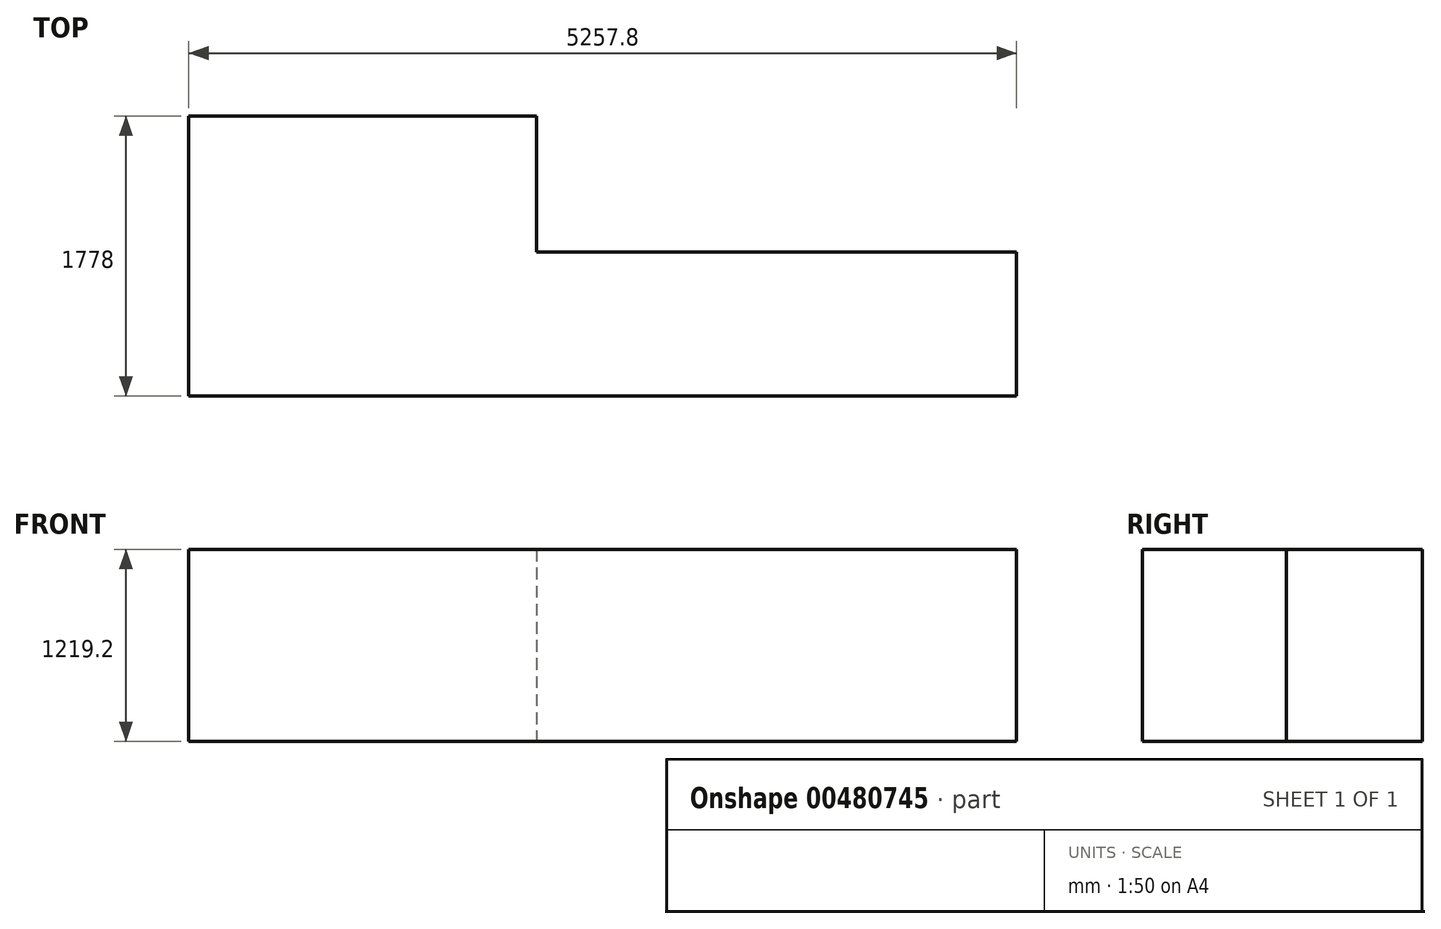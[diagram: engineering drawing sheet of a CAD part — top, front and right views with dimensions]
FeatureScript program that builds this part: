
annotation { "Feature Type Name" : "Feature", "Feature Type Description" : "" }
export const myFeature = defineFeature(function(context is Context, id is Id, definition is map)
    precondition{}
    {
        {
            var Q0;
            Q0=qCreatedBy(makeId("Top.planeOp"),FACE);
            var sketch = newSketch(context, id + "F0", { "sketchPlane" : qUnion([Q0])});
            skLineSegment(sketch, "E0.bottom", {"start": v(1104.9, 889) * mm, "end": v(-1104.9, 889) * mm});
            skLineSegment(sketch, "E0.top", {"start": v(1104.9, -889) * mm, "end": v(-1104.9, -889) * mm});
            skLineSegment(sketch, "E0.left", {"start": v(1104.9, 889) * mm, "end": v(1104.9, 25.4) * mm});
            skLineSegment(sketch, "E0.right", {"start": v(-1104.9, 889) * mm, "end": v(-1104.9, -889) * mm});
            skPoint(sketch, "E0.middle", {"position": v(0, 0) * mm});
            skLineSegment(sketch, "E1", {"start": v(1104.9, -889) * mm, "end": v(4152.9, -889) * mm});
            skLineSegment(sketch, "E2", {"start": v(4152.9, -889) * mm, "end": v(4152.9, 25.4) * mm});
            skLineSegment(sketch, "E3", {"start": v(4152.9, 25.4) * mm, "end": v(1104.9, 25.4) * mm});
            skSolve(sketch);
        }
        {
            var Q0;
            Q0=makeQuery(id+"F0.imprint","IMPRINT",FACE,{"disambiguationData":[TD([[makeQuery(id+"F0.imprint","IMPRINT",EDGE,{"derivedFrom":sQuery(id+"F0.wireOp",EDGE,"E0.bottom")}),1.0]])]});
            extrude(context, id + "F1", {"entities" : qUnion([Q0]), "depth" : 1219.2 * mm});
        }
    });
